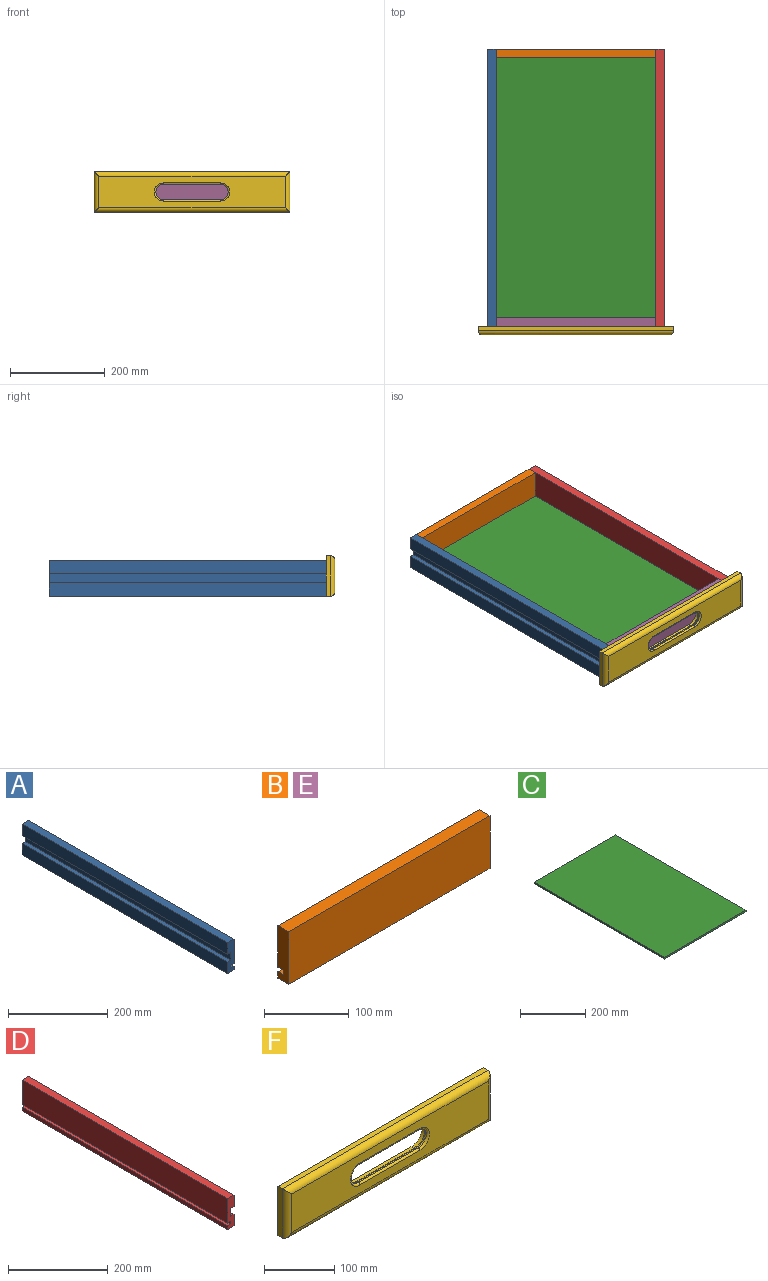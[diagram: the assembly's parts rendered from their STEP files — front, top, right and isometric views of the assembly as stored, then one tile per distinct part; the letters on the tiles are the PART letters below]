
ASSEMBLY  parts=6 mates=5
PART A: 14 faces, bbox 18.3x584.2x76.2 mm
  f0: plane 584.2x9.53mm, normal (0,0,-1), area 5564.5mm2, adj f1,f11,f12,f13
  f1: plane 584.2x19.05mm, normal (-1,0,0), area 11129mm2, adj f0,f2,f12,f13
  f2: plane 584.2x9.53mm, normal (0,0,1), area 5564.5mm2, adj f1,f3,f12,f13
  f3: plane 584.2x28.58mm, normal (-1,0,0), area 16693.5mm2, adj f2,f4,f12,f13
  f4: plane 584.2x18.29mm, normal (0,0,-1), area 10683.8mm2, adj f3,f5,f12,f13
  f5: plane 584.2x9.53mm, normal (1,0,0), area 5564.5mm2, adj f4,f6,f12,f13
  f6: plane 584.2x9.53mm, normal (0,0,1), area 5564.5mm2, adj f5,f7,f12,f13
  f7: plane 584.2x6.35mm, normal (1,0,0), area 3709.7mm2, adj f6,f8,f12,f13
  f8: plane 584.2x9.53mm, normal (0,0,-1), area 5564.5mm2, adj f7,f9,f12,f13
  f9: plane 584.2x60.33mm, normal (1,0,0), area 35241.9mm2, adj f8,f10,f12,f13
  f10: plane 584.2x18.29mm, normal (0,0,1), area 10683.8mm2, adj f9,f11,f12,f13
  f11: plane 584.2x28.58mm, normal (-1,0,0), area 16693.5mm2, adj f0,f10,f12,f13
  f12: plane 76.2x18.29mm, normal (0,1,0), area 1151.6mm2, adj f0,f1,f2,f3,f4,f5,f6,f7
  f13: plane 76.2x18.29mm, normal (0,-1,0), area 1151.6mm2, adj f0,f1,f2,f3,f4,f5,f6,f7
PART B: 10 faces, bbox 336.6x18.3x76.2 mm
  f0: plane 336.55x60.33mm, normal (0,1,0), area 20302.4mm2, adj f1,f2,f3,f7
  f1: plane 76.2x18.29mm, normal (1,0,0), area 1333.1mm2, adj f0,f3,f4,f5,f6,f7,f8,f9
  f2: plane 76.2x18.29mm, normal (-1,0,0), area 1333.1mm2, adj f0,f3,f4,f5,f6,f7,f8,f9
  f3: plane 336.55x18.29mm, normal (0,0,1), area 6154.8mm2, adj f0,f1,f2,f6
  f4: plane 336.55x18.29mm, normal (0,0,-1), area 6154.8mm2, adj f1,f2,f5,f6
  f5: plane 336.55x9.53mm, normal (0,1,0), area 3205.6mm2, adj f1,f2,f4,f9
  f6: plane 336.55x76.2mm, normal (0,-1,0), area 25645.1mm2, adj f1,f2,f3,f4
  f7: plane 336.55x9.53mm, normal (0,0,-1), area 3205.6mm2, adj f0,f1,f2,f8
  f8: plane 336.55x6.35mm, normal (0,1,0), area 2137.1mm2, adj f1,f2,f7,f9
  f9: plane 336.55x9.53mm, normal (0,0,1), area 3205.6mm2, adj f1,f2,f5,f8
PART C: 6 faces, bbox 355.6x566.7x6.4 mm
  f0: plane 355.6x6.35mm, normal (0,1,0), area 2258.1mm2, adj f1,f3,f4,f5
  f1: plane 566.67x355.6mm, normal (0,0,1), area 201509.3mm2, adj f0,f2,f4,f5
  f2: plane 355.6x6.35mm, normal (0,-1,0), area 2258.1mm2, adj f1,f3,f4,f5
  f3: plane 566.67x355.6mm, normal (0,0,-1), area 201509.3mm2, adj f0,f2,f4,f5
  f4: plane 566.67x6.35mm, normal (1,0,0), area 3598.4mm2, adj f0,f1,f2,f3
  f5: plane 566.67x6.35mm, normal (-1,0,0), area 3598.4mm2, adj f0,f1,f2,f3
PART D: 14 faces, bbox 18.3x584.2x76.2 mm
  f0: plane 76.2x18.29mm, normal (0,1,0), area 1151.6mm2, adj f1,f2,f3,f4,f5,f6,f7,f8
  f1: plane 584.2x9.53mm, normal (0,0,-1), area 5564.5mm2, adj f0,f2,f12,f13
  f2: plane 584.2x6.35mm, normal (-1,0,0), area 3709.7mm2, adj f0,f1,f3,f13
  f3: plane 584.2x9.53mm, normal (0,0,1), area 5564.5mm2, adj f0,f2,f4,f13
  f4: plane 584.2x9.53mm, normal (-1,0,0), area 5564.5mm2, adj f0,f3,f5,f13
  f5: plane 584.2x18.29mm, normal (0,0,-1), area 10683.8mm2, adj f0,f4,f6,f13
  f6: plane 584.2x28.58mm, normal (1,0,0), area 16693.5mm2, adj f0,f5,f7,f13
  f7: plane 584.2x9.53mm, normal (0,0,1), area 5564.5mm2, adj f0,f6,f8,f13
  f8: plane 584.2x19.05mm, normal (1,0,0), area 11129mm2, adj f0,f7,f9,f13
  f9: plane 584.2x9.53mm, normal (0,0,-1), area 5564.5mm2, adj f0,f8,f10,f13
  f10: plane 584.2x28.58mm, normal (1,0,0), area 16693.5mm2, adj f0,f9,f11,f13
  f11: plane 584.2x18.29mm, normal (0,0,1), area 10683.8mm2, adj f0,f10,f12,f13
  f12: plane 584.2x60.33mm, normal (-1,0,0), area 35241.9mm2, adj f0,f1,f11,f13
  f13: plane 76.2x18.29mm, normal (0,-1,0), area 1151.6mm2, adj f1,f2,f3,f4,f5,f6,f7,f8
PART E: same geometry as B
PART F: 27 faces, bbox 412.9x18.3x85.7 mm
  f0: plane 120.65x2.41mm, normal (0,0,1), area 291.1mm2, adj f1,f3,f18,f19
  f1: cylinder r=15.88mm len=31.75mm, axis (0,1,0), area 120.3mm2, adj f0,f2,f17,f21
  f2: plane 120.65x2.41mm, normal (0,0,-1), area 291.1mm2, adj f1,f3,f15,f22
  f3: cylinder r=15.88mm len=31.75mm, axis (0,1,0), area 120.3mm2, adj f0,f2,f16,f20
  f4: plane 412.88x85.73mm, normal (0,1,0), area 28479.2mm2, adj f6,f7,f8,f9,f10,f11,f12,f13
  f5: plane 393.83x66.68mm, normal (0,-1,0), area 20521.6mm2, adj f19,f20,f21,f22,f23,f24,f25,f26
  f6: plane 412.88x8.76mm, normal (0,0,-1), area 3618mm2, adj f4,f8,f9,f23
  f7: plane 412.88x8.76mm, normal (0,0,1), area 3618mm2, adj f4,f8,f9,f26
  f8: plane 85.73x8.76mm, normal (1,0,0), area 751.2mm2, adj f4,f6,f7,f24
  f9: plane 85.73x8.76mm, normal (-1,0,0), area 751.2mm2, adj f4,f6,f7,f25
  f10: plane 120.65x9.53mm, normal (0,0,-1), area 1149.2mm2, adj f4,f11,f13,f14
  f11: cylinder r=22.23mm len=44.45mm, axis (0,1,0), area 665.1mm2, adj f4,f10,f12,f14
  f12: plane 120.65x9.53mm, normal (0,0,1), area 1149.2mm2, adj f4,f11,f13,f14
  f13: cylinder r=22.23mm len=44.45mm, axis (0,1,0), area 665.1mm2, adj f4,f10,f12,f14
  f14: plane 165.1x44.45mm, normal (0,1,0), area 1177.8mm2, adj f10,f11,f12,f13,f15,f16,f17,f18
  f15: cylinder r=3.17mm len=120.65mm, axis (1,0,0), area 601.7mm2, adj f2,f14,f16,f17
  f16: torus R=19.05mm, axis (0,1,0), area 266.8mm2, adj f3,f14,f15,f18
  f17: torus R=19.05mm, axis (0,1,0), area 266.8mm2, adj f1,f14,f15,f18
  f18: cylinder r=3.17mm len=120.65mm, axis (-1,0,0), area 601.7mm2, adj f0,f14,f16,f17
  f19: cylinder r=3.17mm len=120.65mm, axis (-1,0,0), area 601.7mm2, adj f0,f5,f20,f21
  f20: torus R=19.05mm, axis (0,-1,0), area 266.8mm2, adj f3,f5,f19,f22
  f21: torus R=19.05mm, axis (0,-1,0), area 266.8mm2, adj f1,f5,f19,f22
  f22: cylinder r=3.17mm len=120.65mm, axis (1,0,0), area 601.7mm2, adj f2,f5,f20,f21
  f23: cylinder r=9.53mm len=412.88mm, axis (-1,0,0), area 6073.8mm2, adj f5,f6,f24,f25
  f24: cylinder r=9.53mm len=85.73mm, axis (0,0,1), area 1179mm2, adj f5,f8,f23,f26
  f25: cylinder r=9.53mm len=85.73mm, axis (0,0,-1), area 1179mm2, adj f5,f9,f23,f26
  f26: cylinder r=9.53mm len=412.88mm, axis (1,0,0), area 6073.8mm2, adj f5,f7,f24,f25
PLACE A t=(12.12,1.23,5.07)mm
PLACE B rot(axis=(0,0,1),180deg) t=(12.12,585.43,5.07)mm
PLACE C t=(12.12,1.23,5.07)mm
PLACE D t=(12.12,1.23,5.07)mm
PLACE E t=(12.12,1.23,5.07)mm fixed
PLACE F t=(12.12,1.23,5.07)mm
MATE fastened A.f13 <-> E.f6  axis (0,-1,0) through (-156.15,1.23,43.17)mm
MATE fastened B.f6 <-> A.f12  axis (0,1,0) through (-156.15,585.43,43.17)mm
MATE fastened F.f6 <-> E.f4  axis (0,0,-1) through (12.12,1.23,-33.03)mm
MATE fastened C.f2 <-> E.f8  axis (0,-1,0) through (12.12,9.99,-20.33)mm
MATE fastened D.f13 <-> E.f6  axis (0,-1,0) through (180.4,1.23,43.17)mm
